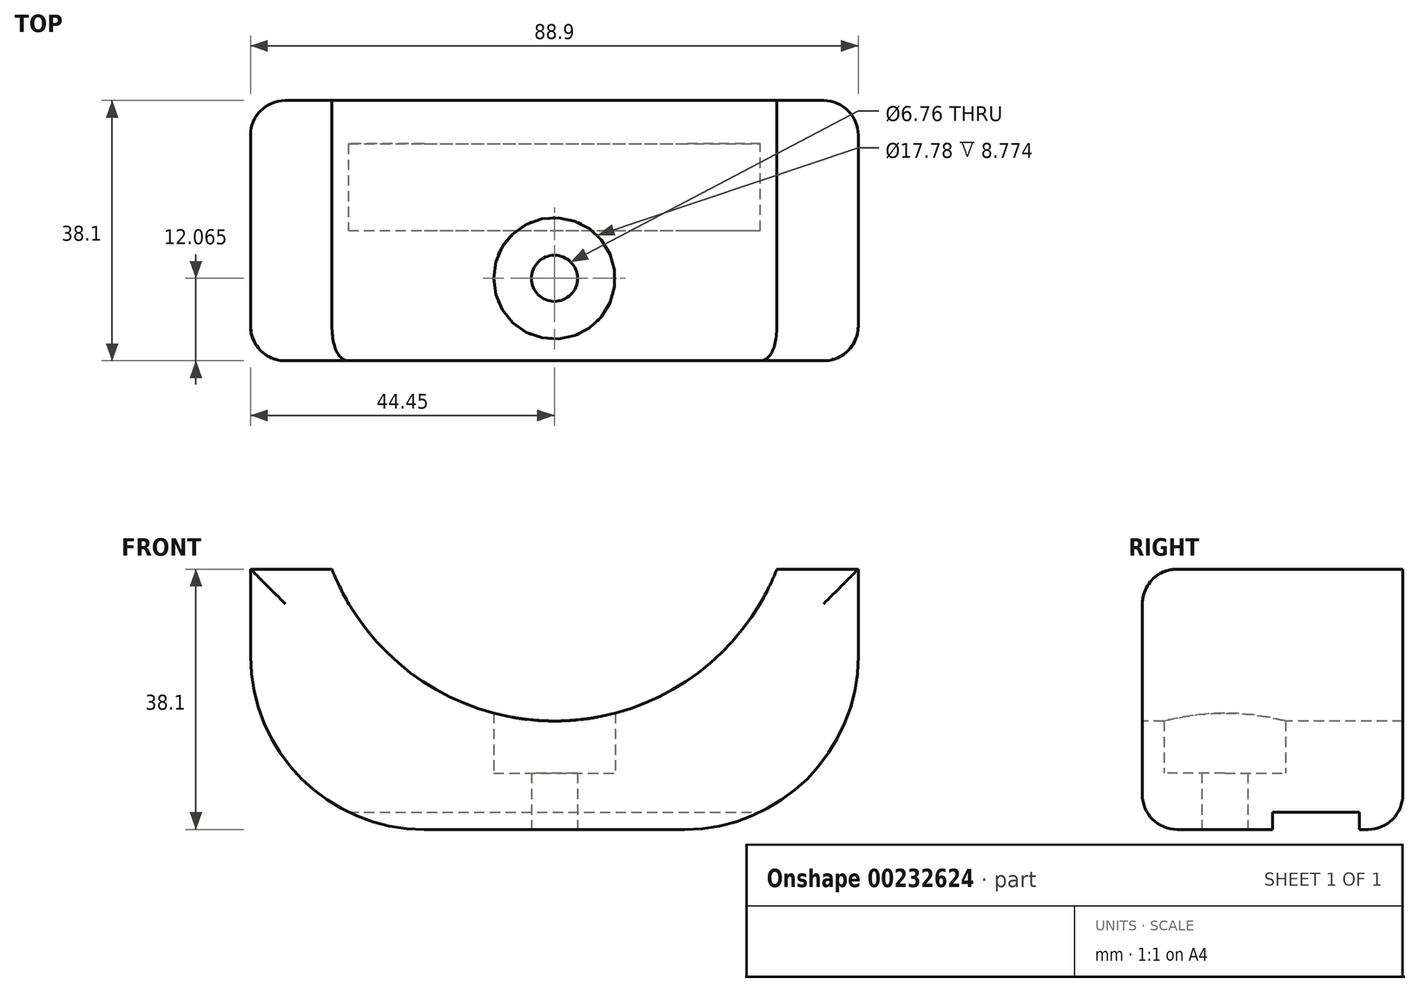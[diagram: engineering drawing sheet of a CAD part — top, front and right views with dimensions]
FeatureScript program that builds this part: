
annotation { "Feature Type Name" : "Feature", "Feature Type Description" : "" }
export const myFeature = defineFeature(function(context is Context, id is Id, definition is map)
    precondition{}
    {
        {
            var Q0;
            Q0=qCreatedBy(makeId("Front.planeOp"),FACE);
            var sketch = newSketch(context, id + "F0", { "sketchPlane" : qUnion([Q0])});
            skLineSegment(sketch, "E0.bottom", {"start": v(0, 0) * mm, "end": v(88.9, 0) * mm});
            skLineSegment(sketch, "E0.top", {"start": v(0, 50.8) * mm, "end": v(88.9, 50.8) * mm});
            skLineSegment(sketch, "E0.left", {"start": v(0, 0) * mm, "end": v(0, 50.8) * mm});
            skLineSegment(sketch, "E0.right", {"start": v(88.9, 0) * mm, "end": v(88.9, 50.8) * mm});
            skSolve(sketch);
        }
        {
            var Q0;
            Q0 = qSketchRegion(id + "F0", true);
            extrude(context, id + "F1", {"entities" : qUnion([Q0]), "depth" : 38.1 * mm});
        }
        {
            var Q0;
            Q0=makeQuery(id+"F1.opExtrude","CAP_FACE",FACE,{"disambiguationData":[OSD([sQuery(id+"F0.wireOp",EDGE,"E0.bottom"),sQuery(id+"F0.wireOp",EDGE,"E0.top"),sQuery(id+"F0.wireOp",EDGE,"E0.left"),sQuery(id+"F0.wireOp",EDGE,"E0.right")])],"isStart":false});
            var sketch = newSketch(context, id + "F2", { "sketchPlane" : qUnion([Q0])});
            skLineSegment(sketch, "E1", {"start": v(44.45, 0) * mm, "end": v(44.45, 15.88) * mm});
            skLineSegment(sketch, "E2", {"start": v(44.45, 15.88) * mm, "end": v(44.45, 50.8) * mm});
            skCircle(sketch, "E3", {"center": v(44.45, 50.8) * mm, "radius": 34.93 * mm});
            skSolve(sketch);
        }
        {
            var Q0;
            {var subQ0=sQuery(id+"F2.wireOp",EDGE,"E2");Q0=makeQuery(id+"F2.imprint","IMPRINT",FACE,{"disambiguationData":[TD([[makeQuery(id+"F2.imprint","IMPRINT",EDGE,{"derivedFrom":subQ0}),1.0]])]});}
            var Q1;
            {var subQ0=sQuery(id+"F2.wireOp",EDGE,"E2");Q1=makeQuery(id+"F2.imprint","IMPRINT",FACE,{"disambiguationData":[TD([[makeQuery(id+"F2.imprint","IMPRINT",EDGE,{"derivedFrom":subQ0}),-1.0]])]});}
            extrude(context, id + "F3", {"entities" : qUnion([Q0, Q1]), "operationType" : NewBodyOperationType.REMOVE, "endBound" : BoundingType.THROUGH_ALL, "oppositeDirection" : true, "depth" : 25.4 * mm});
        }
        {
            var Q0;
            Q0=makeQuery(id+"F1.opExtrude","SWEPT_FACE",FACE,{"disambiguationData":[OSD([sQuery(id+"F0.wireOp",EDGE,"E0.bottom")])]});
            var sketch = newSketch(context, id + "F4", { "sketchPlane" : qUnion([Q0])});
            skLineSegment(sketch, "E4", {"start": v(44.45, 38.1) * mm, "end": v(44.45, 26.04) * mm});
            skPoint(sketch, "E4.endSnap0", {"position": v(44.45, 38.1) * mm});
            skCircle(sketch, "E5", {"center": v(44.45, 26.04) * mm, "radius": 8.9 * mm});
            skCircle(sketch, "E6", {"center": v(44.45, 26.04) * mm, "radius": 3.38 * mm});
            skSolve(sketch);
        }
        {
            var Q0;
            Q0=makeQuery(id+"F4.imprint","IMPRINT",FACE,{"disambiguationData":[TD([[makeQuery(id+"F4.imprint","IMPRINT",EDGE,{"derivedFrom":sQuery(id+"F4.wireOp",EDGE,"E6")}),1.0]])]});
            extrude(context, id + "F5", {"entities" : qUnion([Q0]), "operationType" : NewBodyOperationType.REMOVE, "oppositeDirection" : true, "depth" : 25.4 * mm});
        }
        {
            var Q0;
            Q0=qCreatedBy(makeId("Top.planeOp"),FACE);
            cPlane(context, id + "F6", {"entities" : qUnion([Q0]), "cplaneType" : CPlaneType.OFFSET, "offset" : 9.52 * mm, "width" : 152.4 * mm, "height" : 152.4 * mm});
        }
        {
            var Q0;
            Q0=qCreatedBy(id+"F6.planeOp",FACE);
            var sketch = newSketch(context, id + "F7", { "sketchPlane" : qUnion([Q0])});
            skCircle(sketch, "E7", {"center": v(44.45, -26.03) * mm, "radius": 8.9 * mm});
            skSolve(sketch);
        }
        {
            var Q0;
            Q0 = qSketchRegion(id + "F7", true);
            extrude(context, id + "F8", {"entities" : qUnion([Q0]), "operationType" : NewBodyOperationType.REMOVE, "depth" : 25.4 * mm});
        }
        {
            var Q0;
            Q0=makeQuery(id+"F1.opExtrude","SWEPT_FACE",FACE,{"disambiguationData":[OSD([sQuery(id+"F0.wireOp",EDGE,"E0.right")])]});
            var sketch = newSketch(context, id + "F9", { "sketchPlane" : qUnion([Q0])});
            skLineSegment(sketch, "E8", {"start": v(-6.35, 0) * mm, "end": v(-6.35, 2.55) * mm});
            skLineSegment(sketch, "E9", {"start": v(-6.35, 2.55) * mm, "end": v(-19.06, 2.55) * mm});
            skLineSegment(sketch, "E10", {"start": v(-19.06, 2.55) * mm, "end": v(-19.06, 0) * mm});
            skLineSegment(sketch, "E11", {"start": v(-19.06, 0) * mm, "end": v(-6.35, 0) * mm});
            skSolve(sketch);
        }
        {
            var Q0;
            Q0 = qSketchRegion(id + "F9", true);
            extrude(context, id + "F10", {"entities" : qUnion([Q0]), "operationType" : NewBodyOperationType.REMOVE, "oppositeDirection" : true, "depth" : 207.52 * mm});
        }
        {
            var Q0;
            Q0=makeQuery(id+"F1.opExtrude","SWEPT_EDGE",EDGE,{"disambiguationData":[OSD([sQuery(id+"F0.wireOp",EDGE,"E0.bottom"),sQuery(id+"F0.wireOp",EDGE,"E0.right")])]});
            var Q1;
            Q1=makeQuery(id+"F1.opExtrude","SWEPT_EDGE",EDGE,{"disambiguationData":[OSD([sQuery(id+"F0.wireOp",EDGE,"E0.bottom"),sQuery(id+"F0.wireOp",EDGE,"E0.left")])]});
            fillet(context, id + "F11", {"entities" : qUnion([Q0, Q1]), "radius" : 25.4 * mm, "tangentPropagation" : true, "allowEdgeOverflow" : false});
        }
        {
            var Q0;
            Q0=makeQuery(id+"F1.opExtrude","CAP_FACE",FACE,{"disambiguationData":[OSD([sQuery(id+"F0.wireOp",EDGE,"E0.bottom"),sQuery(id+"F0.wireOp",EDGE,"E0.top"),sQuery(id+"F0.wireOp",EDGE,"E0.left"),sQuery(id+"F0.wireOp",EDGE,"E0.right")])],"isStart":true});
            var sketch = newSketch(context, id + "F12", { "sketchPlane" : qUnion([Q0])});
            skLineSegment(sketch, "E12", {"start": v(-88.9, 50.8) * mm, "end": v(-88.9, 38.1) * mm});
            skLineSegment(sketch, "E13", {"start": v(-88.9, 38.1) * mm, "end": v(0, 38.1) * mm});
            skLineSegment(sketch, "E14", {"start": v(0, 38.1) * mm, "end": v(0, 50.8) * mm});
            skLineSegment(sketch, "E15", {"start": v(0, 50.8) * mm, "end": v(-88.9, 50.8) * mm});
            skSolve(sketch);
        }
        {
            var Q0;
            Q0 = qSketchRegion(id + "F12", true);
            extrude(context, id + "F13", {"entities" : qUnion([Q0]), "operationType" : NewBodyOperationType.REMOVE, "oppositeDirection" : true, "depth" : 56.64 * mm});
        }
        {
            var Q0;
            Q0=makeQuery(id+"F13.boolean.opBoolean","COPY",EDGE,{"derivedFrom":makeQuery(id+"F13.opExtrude","SWEPT_EDGE",EDGE,{"disambiguationData":[OSD([sQuery(id+"F0.wireOp",EDGE,"E0.left"),sQuery(id+"F12.wireOp",EDGE,"E13"),sQuery(id+"F12.wireOp",EDGE,"E14")])]})});
            var Q1;
            Q1=makeQuery(id+"F13.boolean.opBoolean","COPY",EDGE,{"derivedFrom":makeQuery(id+"F13.opExtrude","SWEPT_EDGE",EDGE,{"disambiguationData":[OSD([sQuery(id+"F0.wireOp",EDGE,"E0.right"),sQuery(id+"F12.wireOp",EDGE,"E12"),sQuery(id+"F12.wireOp",EDGE,"E13")])]})});
            var Q2;
            {var subQ0=sQuery(id+"F0.wireOp",EDGE,"E0.left");var subQ1=sQuery(id+"F0.wireOp",EDGE,"E0.bottom");Q2=makeQuery(id+"F11.opFillet","BLEND_EDGE",EDGE,{"blendedFrom":[makeQuery(id+"F1.opExtrude","SWEPT_EDGE",EDGE,{"disambiguationData":[OSD([subQ1,subQ0])]}),makeQuery(id+"F1.opExtrude","CAP_FACE",FACE,{"disambiguationData":[OSD([subQ1,sQuery(id+"F0.wireOp",EDGE,"E0.top"),subQ0,sQuery(id+"F0.wireOp",EDGE,"E0.right")])],"isStart":false})],"blendedInto":[makeQuery(id+"F1.opExtrude","CAP_FACE",FACE,{"disambiguationData":[OSD([subQ1,sQuery(id+"F0.wireOp",EDGE,"E0.top"),subQ0,sQuery(id+"F0.wireOp",EDGE,"E0.right")])],"isStart":false})]});}
            var Q3;
            {var subQ0=sQuery(id+"F0.wireOp",EDGE,"E0.left");var subQ1=sQuery(id+"F0.wireOp",EDGE,"E0.bottom");Q3=makeQuery(id+"F11.opFillet","BLEND_EDGE",EDGE,{"blendedFrom":[makeQuery(id+"F1.opExtrude","SWEPT_EDGE",EDGE,{"disambiguationData":[OSD([subQ1,subQ0])]}),makeQuery(id+"F1.opExtrude","CAP_FACE",FACE,{"disambiguationData":[OSD([subQ1,sQuery(id+"F0.wireOp",EDGE,"E0.top"),subQ0,sQuery(id+"F0.wireOp",EDGE,"E0.right")])],"isStart":true})],"blendedInto":[makeQuery(id+"F1.opExtrude","CAP_FACE",FACE,{"disambiguationData":[OSD([subQ1,sQuery(id+"F0.wireOp",EDGE,"E0.top"),subQ0,sQuery(id+"F0.wireOp",EDGE,"E0.right")])],"isStart":true})]});}
            var Q4;
            Q4=makeQuery(id+"F13.boolean.opBoolean","INTERSECT",EDGE,{"disambiguationData":[OD(1.0)],"derivedFrom":[makeQuery(id+"F1.opExtrude","CAP_FACE",FACE,{"disambiguationData":[OSD([sQuery(id+"F0.wireOp",EDGE,"E0.bottom"),sQuery(id+"F0.wireOp",EDGE,"E0.top"),sQuery(id+"F0.wireOp",EDGE,"E0.left"),sQuery(id+"F0.wireOp",EDGE,"E0.right")])],"isStart":false}),makeQuery(id+"F13.opExtrude","SWEPT_FACE",FACE,{"disambiguationData":[OSD([sQuery(id+"F12.wireOp",EDGE,"E13")])]})]});
            var Q5;
            {var subQ0=sQuery(id+"F0.wireOp",EDGE,"E0.left");var subQ1=sQuery(id+"F12.wireOp",EDGE,"E13");Q5=makeQuery(id+"F13.boolean.opBoolean","COPY",EDGE,{"disambiguationData":[TD([makeQuery(id+"F1.opExtrude","SWEPT_FACE",FACE,{"disambiguationData":[OSD([subQ0])]})])],"derivedFrom":makeQuery(id+"F13.opExtrude","CAP_EDGE",EDGE,{"disambiguationData":[OSD([subQ1])],"isStart":true})});}
            var Q6;
            Q6=makeQuery(id+"F13.boolean.opBoolean","INTERSECT",EDGE,{"disambiguationData":[OD(0.0)],"derivedFrom":[makeQuery(id+"F1.opExtrude","CAP_FACE",FACE,{"disambiguationData":[OSD([sQuery(id+"F0.wireOp",EDGE,"E0.bottom"),sQuery(id+"F0.wireOp",EDGE,"E0.top"),sQuery(id+"F0.wireOp",EDGE,"E0.left"),sQuery(id+"F0.wireOp",EDGE,"E0.right")])],"isStart":false}),makeQuery(id+"F13.opExtrude","SWEPT_FACE",FACE,{"disambiguationData":[OSD([sQuery(id+"F12.wireOp",EDGE,"E13")])]})]});
            var Q7;
            {var subQ0=sQuery(id+"F0.wireOp",EDGE,"E0.right");var subQ1=sQuery(id+"F12.wireOp",EDGE,"E13");Q7=makeQuery(id+"F13.boolean.opBoolean","COPY",EDGE,{"disambiguationData":[TD([makeQuery(id+"F1.opExtrude","SWEPT_FACE",FACE,{"disambiguationData":[OSD([subQ0])]})])],"derivedFrom":makeQuery(id+"F13.opExtrude","CAP_EDGE",EDGE,{"disambiguationData":[OSD([subQ1])],"isStart":true})});}
            fillet(context, id + "F14", {"entities" : qUnion([Q0, Q1, Q2, Q3, Q4, Q5, Q6, Q7]), "radius" : 5.08 * mm, "tangentPropagation" : true, "allowEdgeOverflow" : false});
        }
        {
            var Q0;
            Q0=makeQuery(id+"F8.boolean.opBoolean","COPY",FACE,{"derivedFrom":makeQuery(id+"F8.opExtrude","CAP_FACE",FACE,{"disambiguationData":[OSD([sQuery(id+"F7.wireOp",EDGE,"E7")])],"isStart":true})});
            extrude(context, id + "F15", {"entities" : qUnion([Q0]), "operationType" : NewBodyOperationType.REMOVE, "oppositeDirection" : true, "depth" : 1.27 * mm});
        }
    });
